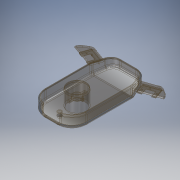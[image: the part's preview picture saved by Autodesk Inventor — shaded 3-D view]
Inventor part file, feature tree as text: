
AUTODESK INVENTOR PART (.ipt)
format: ipt  version: 2019 (Build 230136000, 136)  size: 678,400 bytes
history: native  units: mm
features: extrude x18, sketch x17, projected_geometry x8, plane x7, fillet x6, other x5, mirror x5, loft x1, shell x1, split x1, sweep x1, surface_op x1
ambient origin geometry x8: Origin, YZ Plane, XZ Plane, XY Plane, X Axis, Y Axis, Z Axis, Center Point
bodies: Body1 (feature_tree), Body2 (feature_tree), Body3 (feature_tree), Body4 (feature_tree), Body5 (feature_tree)
feature tree (71):
  other  "ROV Hull - Bottom"
  extrude  "Extrusion1"  Depth=90.0mm
  plane  "Work Plane2"
  loft  "Loft2"
  fillet  "Fillet1"  Radius=180.0mm
  fillet  "Fillet2"  [1 undecoded]
  fillet  "Fillet3"  [1 undecoded]
  fillet  "Fillet4"  Radius=60.0mm
  shell  "Shell2"  Thickness=50.0mm
  extrude  "Extrusion2"  Depth=16.0mm
  other  "Lip1"
  other  "Lip2"
  split  "Split1"
  sketch  "Sketch10"  dims[d33=50.0mm d34=16.0mm]
  extrude  "Extrusion5"  Depth=10.0mm
  extrude  "Extrusion6"  Depth=30.0mm TaperAngle=0.0deg
  sketch  "Sketch12"  dims[d47=90.0mm d48=0.0mm]
  plane  "Work Plane3"
  mirror  "Mirror1"
  plane  "Work Plane4"
  plane  "Work Plane5"
  extrude  "Extrusion12"  Depth=140.0mm TaperAngle=0.0deg
  plane  "Work Plane6"
  plane  "Work Plane7"
  extrude  "Extrusion15"  Depth=70.0mm
  extrude  "Extrusion16"  [1 undecoded]
  extrude  "Extrusion18"  TaperAngle=0.0deg  [1 undecoded]
  extrude  "Extrusion19"  Depth=25.0mm
  fillet  "Fillet8"  Radius=18.0mm
  mirror  "Mirror5"
  extrude  "Extrusion20"  Depth=5.0mm
  plane  "Work Plane8"
  extrude  "Extrusion22"  [1 undecoded]
  fillet  "Fillet10"  Radius=60.0mm
  mirror  "Mirror6"
  extrude  "Extrusion23"  Depth=57.0mm TaperAngle=0.0deg
  extrude  "Extrusion24"  Depth=2.0mm
  sweep  "Sweep1"
  extrude  "Extrusion25"  Depth=12.0mm TaperAngle=0.0deg
  mirror  "Mirror7"
  extrude  "Extrusion26"  Depth=17.0mm
  extrude  "Extrusion27"  Depth=12.0mm TaperAngle=0.0deg
  mirror  "Mirror8"
  extrude  "Extrusion28"  Depth=3.0mm
  extrude  "Extrusion29"  Depth=12.0mm TaperAngle=0.0deg
  sketch  "Sketch1"  dims[d8=250.0mm d10=90.0mm]
  sketch  "Sketch5"  dims[d11=60.0mm d12=0.0mm d22=100.0mm d24=180.0mm d26=0.0mm d27=90.0deg d28=0.0mm d29=90.0deg d30=60.0mm d32=50.0mm]
  other  "Edges1"
  projected_geometry  "Projected Loop9"
  sketch  "Sketch11"  dims[d35=10.0mm d36=360.0mm]
  projected_geometry  "Projected Loop12"
  sketch  "Sketch18"  dims[d55=10.0mm d56=4.0mm d57=0.0mm d58=0.0mm d59=0.349066mm d60=0.0mm]
  other  "Srf3"
  sketch  "Sketch20"  dims[d62=10.0mm d63=4.0mm d64=0.0mm d65=0.0mm d66=0.349066mm d67=0.0mm d77=30.0mm d78=0.0mm]
  projected_geometry  "Projected Loop19"
  projected_geometry  "Projected Loop20"
  projected_geometry  "Projected Loop25"
  sketch  "Sketch26"  dims[d83=5.0mm d84=140.0mm d85=0.0mm]
  sketch  "Sketch27"  dims[d94=-125.0mm d95=70.0mm]
  sketch  "Sketch28"  dims[d96=39.0mm d97=-405.0mm]
  sketch  "Sketch29"  dims[d124=10.0mm d125=0.0mm d133=0.0mm]
  sketch  "Sketch30"  dims[d135=344.0mm d139=25.0mm d140=18.0mm]
  sketch  "Sketch31"  dims[d143=5.0mm d144=5.0mm]
  projected_geometry  "Projected Loop28"
  sketch  "Sketch32"  dims[d162=2.5mm d173=5.0mm d174=0.0mm d175=-5.0mm d176=60.0mm d177=0.0mm]
  projected_geometry  "Projected Loop30"
  sketch  "Sketch33"  dims[d178=20.0mm d179=0.0mm d187=57.0mm d188=0.0mm]
  sketch  "Sketch34"  dims[d191=40.0mm d192=0.0mm d193=2.0mm]
  sketch  "Sketch35"  dims[d194=12.0mm d195=8.0mm d196=65.0mm d197=0.0mm d198=17.0mm d206=4.0mm d207=0.0mm d208=3.0mm d212=11.0mm d213=0.0mm d214=100.0mm d215=12.0mm d216=0.0mm d217=90.0mm d218=5.0mm d220=13.0mm d221=0.0mm d222=0.0mm d226=10.0mm d227=6.954mm d228=6.0mm d229=6.954mm d230=6.0mm d231=5.0mm d232=0.0mm d234=6.0mm d235=70.0mm d236=0.0mm d237=6.0mm d238=5.0mm d239=8.0mm d240=0.0mm d241=0.0mm d242=52.0mm d243=46.5mm d252=10.0mm d253=10.0mm d255=12.0mm d256=0.0mm d257=4.0mm d258=11.0mm d259=0.0mm]
  projected_geometry  "Projected Loop31"
  surface_op  "Boundary Patch3"
note: 5 required parameter values undecoded (feature->parameter linkage not recoverable at this tier; creation-order binding heuristic only, values carry confidence <= 0.55)
